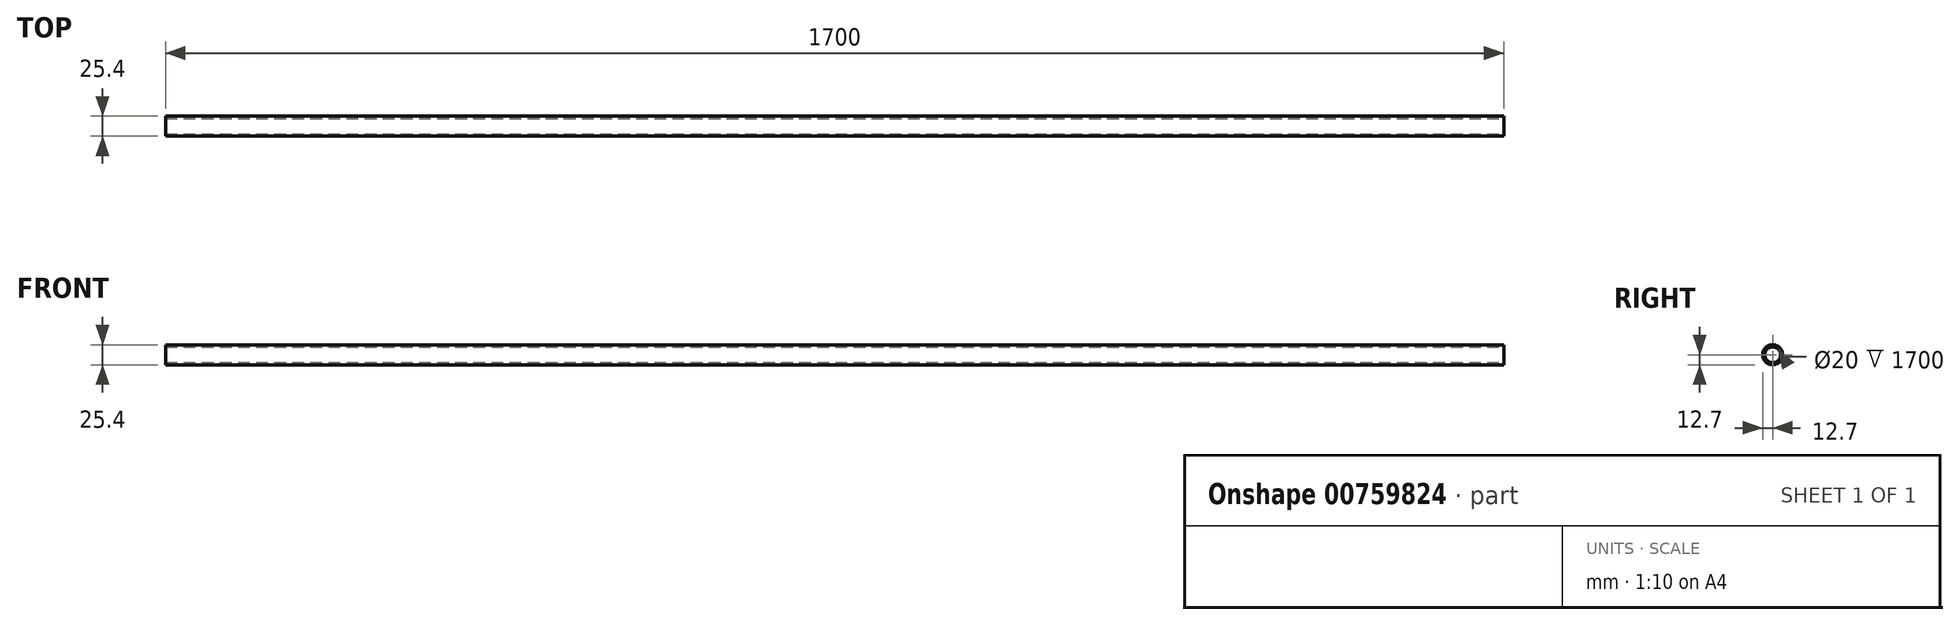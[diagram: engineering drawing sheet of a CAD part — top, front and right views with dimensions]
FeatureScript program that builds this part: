
annotation { "Feature Type Name" : "Feature", "Feature Type Description" : "" }
export const myFeature = defineFeature(function(context is Context, id is Id, definition is map)
    precondition{}
    {
        {
            var Q0;
            Q0=qCreatedBy(makeId("Right.planeOp"),FACE);
            var sketch = newSketch(context, id + "F0", { "sketchPlane" : qUnion([Q0])});
            skCircle(sketch, "E0", {"center": v(0, 0) * mm, "radius": 12.7 * mm});
            skCircle(sketch, "E1", {"center": v(0, 0) * mm, "radius": 10 * mm});
            skSolve(sketch);
        }
        {
            var Q0;
            Q0=makeQuery(id+"F0.imprint","IMPRINT",FACE,{"disambiguationData":[TD([[makeQuery(id+"F0.imprint","IMPRINT",EDGE,{"derivedFrom":sQuery(id+"F0.wireOp",EDGE,"E0")}),1.0]])]});
            extrude(context, id + "F1", {"entities" : qUnion([Q0]), "oppositeDirection" : true, "depth" : 1700 * mm, "offsetDistance" : 25 * mm});
        }
    });
